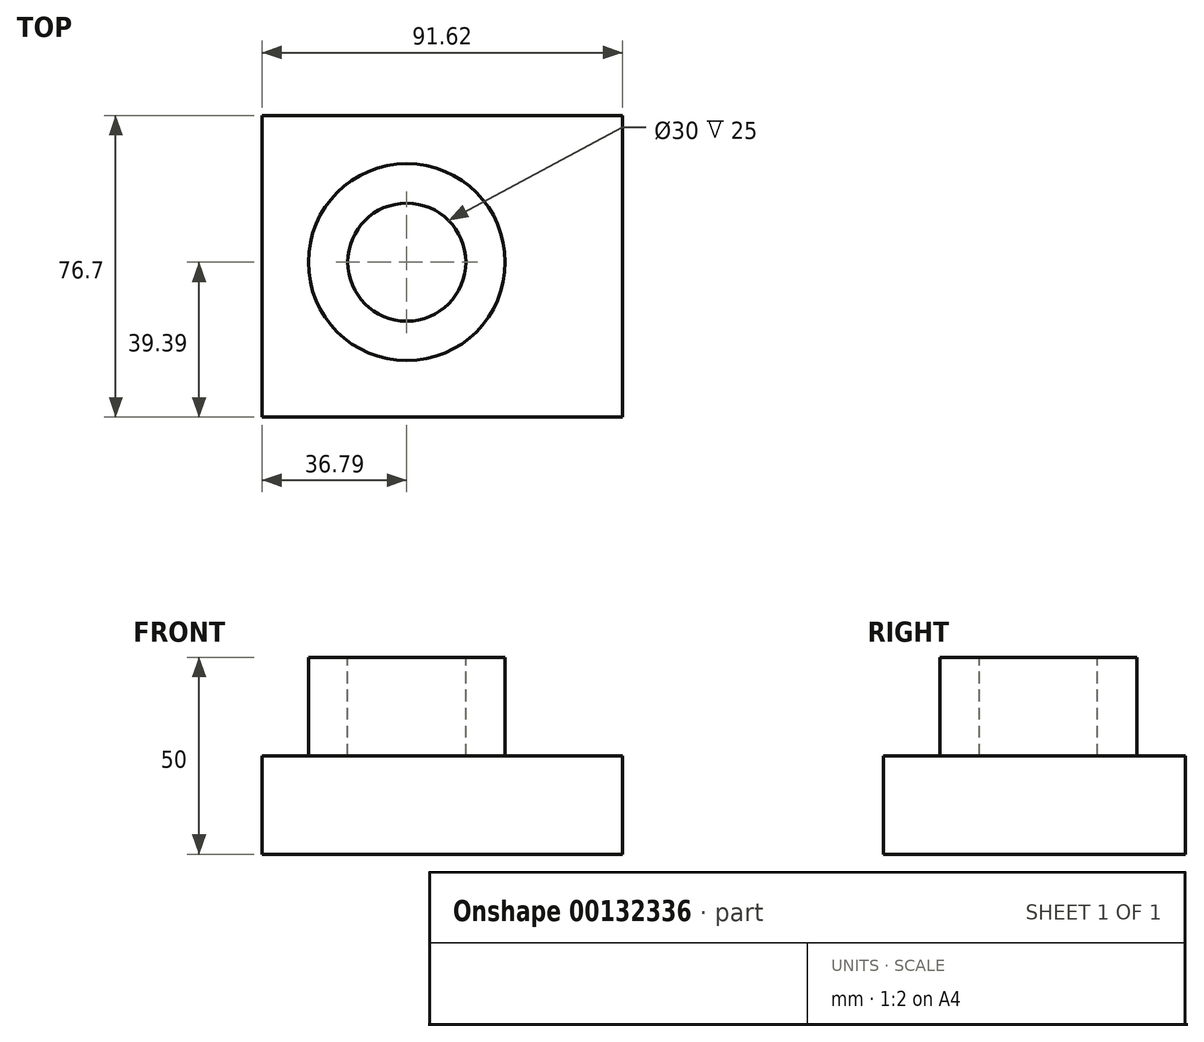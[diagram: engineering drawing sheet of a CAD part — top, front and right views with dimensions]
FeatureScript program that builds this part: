
annotation { "Feature Type Name" : "Feature", "Feature Type Description" : "" }
export const myFeature = defineFeature(function(context is Context, id is Id, definition is map)
    precondition{}
    {
        {
            var Q0;
            Q0=qCreatedBy(makeId("Top.planeOp"),FACE);
            var sketch = newSketch(context, id + "F0", { "sketchPlane" : qUnion([Q0])});
            skCircle(sketch, "E0", {"center": v(0, 0) * mm, "radius": 25 * mm});
            skSolve(sketch);
        }
        {
            var Q0;
            Q0 = qSketchRegion(id + "F0", true);
            extrude(context, id + "F1", {"entities" : qUnion([Q0]), "depth" : 50 * mm});
        }
        {
            var Q0;
            Q0=makeQuery(id+"F1.opExtrude","CAP_FACE",FACE,{"disambiguationData":[OSD([sQuery(id+"F0.wireOp",EDGE,"E0")])],"isStart":false});
            var sketch = newSketch(context, id + "F2", { "sketchPlane" : qUnion([Q0])});
            skCircle(sketch, "E1", {"center": v(0, 0) * mm, "radius": 15 * mm});
            skSolve(sketch);
        }
        {
            var Q0;
            Q0 = qSketchRegion(id + "F2", true);
            extrude(context, id + "F3", {"entities" : qUnion([Q0]), "operationType" : NewBodyOperationType.REMOVE, "endBound" : BoundingType.THROUGH_ALL, "oppositeDirection" : true, "depth" : 25 * mm});
        }
        {
            var Q0;
            Q0=qCreatedBy(makeId("Top.planeOp"),FACE);
            var sketch = newSketch(context, id + "F4", { "sketchPlane" : qUnion([Q0])});
            skLineSegment(sketch, "E2.bottom", {"start": v(-36.79, 37.3) * mm, "end": v(54.83, 37.3) * mm});
            skLineSegment(sketch, "E2.top", {"start": v(-36.79, -39.39) * mm, "end": v(54.83, -39.39) * mm});
            skLineSegment(sketch, "E2.left", {"start": v(-36.79, 37.3) * mm, "end": v(-36.79, -39.39) * mm});
            skLineSegment(sketch, "E2.right", {"start": v(54.83, 37.3) * mm, "end": v(54.83, -39.39) * mm});
            skSolve(sketch);
        }
        {
            var Q0;
            Q0 = qSketchRegion(id + "F4", true);
            extrude(context, id + "F5", {"entities" : qUnion([Q0]), "operationType" : NewBodyOperationType.ADD, "depth" : 25 * mm});
        }
    });
